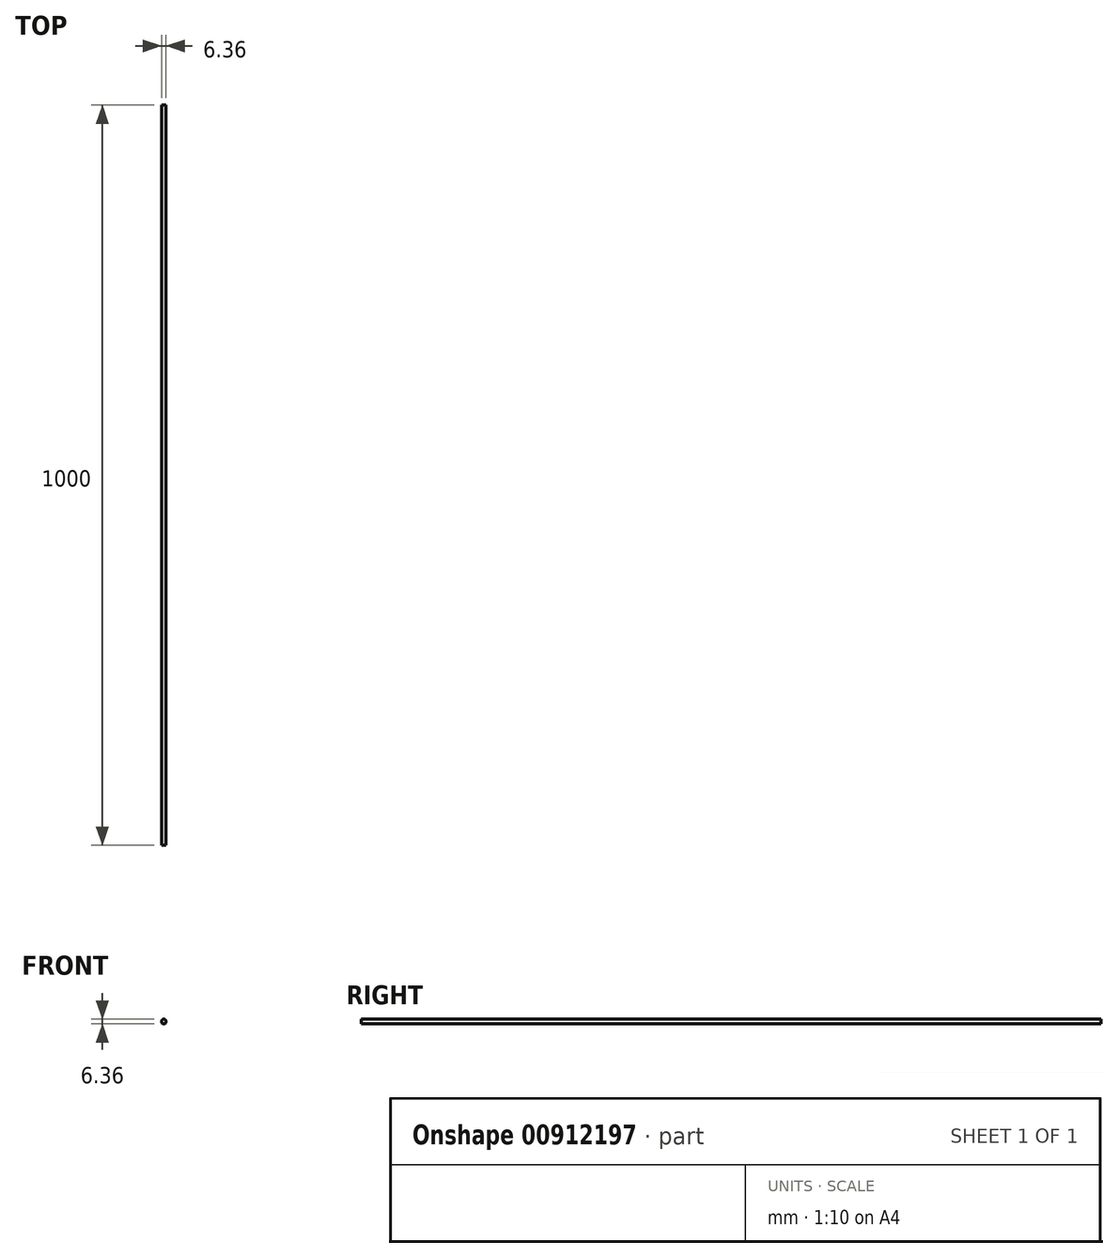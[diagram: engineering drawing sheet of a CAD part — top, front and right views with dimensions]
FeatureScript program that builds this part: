
annotation { "Feature Type Name" : "Feature", "Feature Type Description" : "" }
export const myFeature = defineFeature(function(context is Context, id is Id, definition is map)
    precondition{}
    {
        {
            var Q0;
            Q0=qCreatedBy(makeId("Front.planeOp"),FACE);
            var sketch = newSketch(context, id + "F0", { "sketchPlane" : qUnion([Q0])});
            skCircle(sketch, "E0", {"center": v(0, 0) * mm, "radius": 3.18 * mm});
            skSolve(sketch);
        }
        {
            var Q0;
            Q0 = qSketchRegion(id + "F0", true);
            extrude(context, id + "F1", {"entities" : qUnion([Q0]), "depth" : 1000 * mm, "offsetDistance" : 25 * mm});
        }
    });
